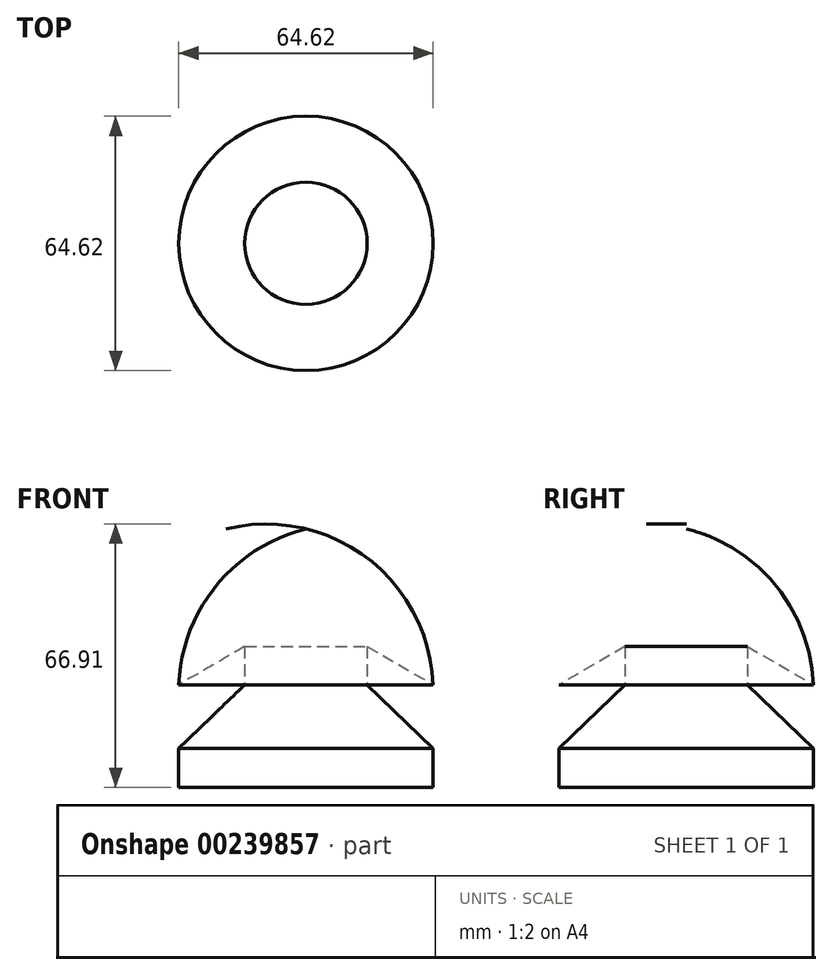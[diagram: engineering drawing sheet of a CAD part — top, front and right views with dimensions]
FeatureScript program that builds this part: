
annotation { "Feature Type Name" : "Feature", "Feature Type Description" : "" }
export const myFeature = defineFeature(function(context is Context, id is Id, definition is map)
    precondition{}
    {
        {
            var Q0;
            Q0=qCreatedBy(makeId("Front.planeOp"),FACE);
            var sketch = newSketch(context, id + "F0", { "sketchPlane" : qUnion([Q0])});
            skLineSegment(sketch, "E0", {"start": v(0, 0) * mm, "end": v(-32.3, 0) * mm});
            skLineSegment(sketch, "E1", {"start": v(-32.3, 0) * mm, "end": v(-32.3, 9.9) * mm});
            skLineSegment(sketch, "E2", {"start": v(-32.3, 9.9) * mm, "end": v(-15.54, 26.06) * mm});
            skLineSegment(sketch, "E3", {"start": v(-15.54, 26.06) * mm, "end": v(-15.54, 35.81) * mm});
            skLineSegment(sketch, "E4", {"start": v(-15.54, 35.81) * mm, "end": v(-32.3, 26.06) * mm});
            skLineSegment(sketch, "E5", {"start": v(0, 0) * mm, "end": v(0, 65.68) * mm});
            skArc(sketch, "E6", {"start": v(0, 65.68) * mm, "mid": v(-22.79, 51.28) * mm, "end": v(-32.3, 26.06) * mm});
            skSolve(sketch);
        }
        {
            var Q0;
            Q0=makeQuery(id+"F0.imprint","IMPRINT",FACE,{"disambiguationData":[TD([[makeQuery(id+"F0.imprint","IMPRINT",EDGE,{"derivedFrom":sQuery(id+"F0.wireOp",EDGE,"E0")}),-1.0]])]});
            var Q1;
            Q1=sQuery(id+"F0.wireOp",EDGE,"E5");
            revolve(context, id + "F1", {"entities" : qUnion([Q0]), "axis" : qUnion([Q1]), "revolveType" : RevolveType.FULL});
        }
    });
